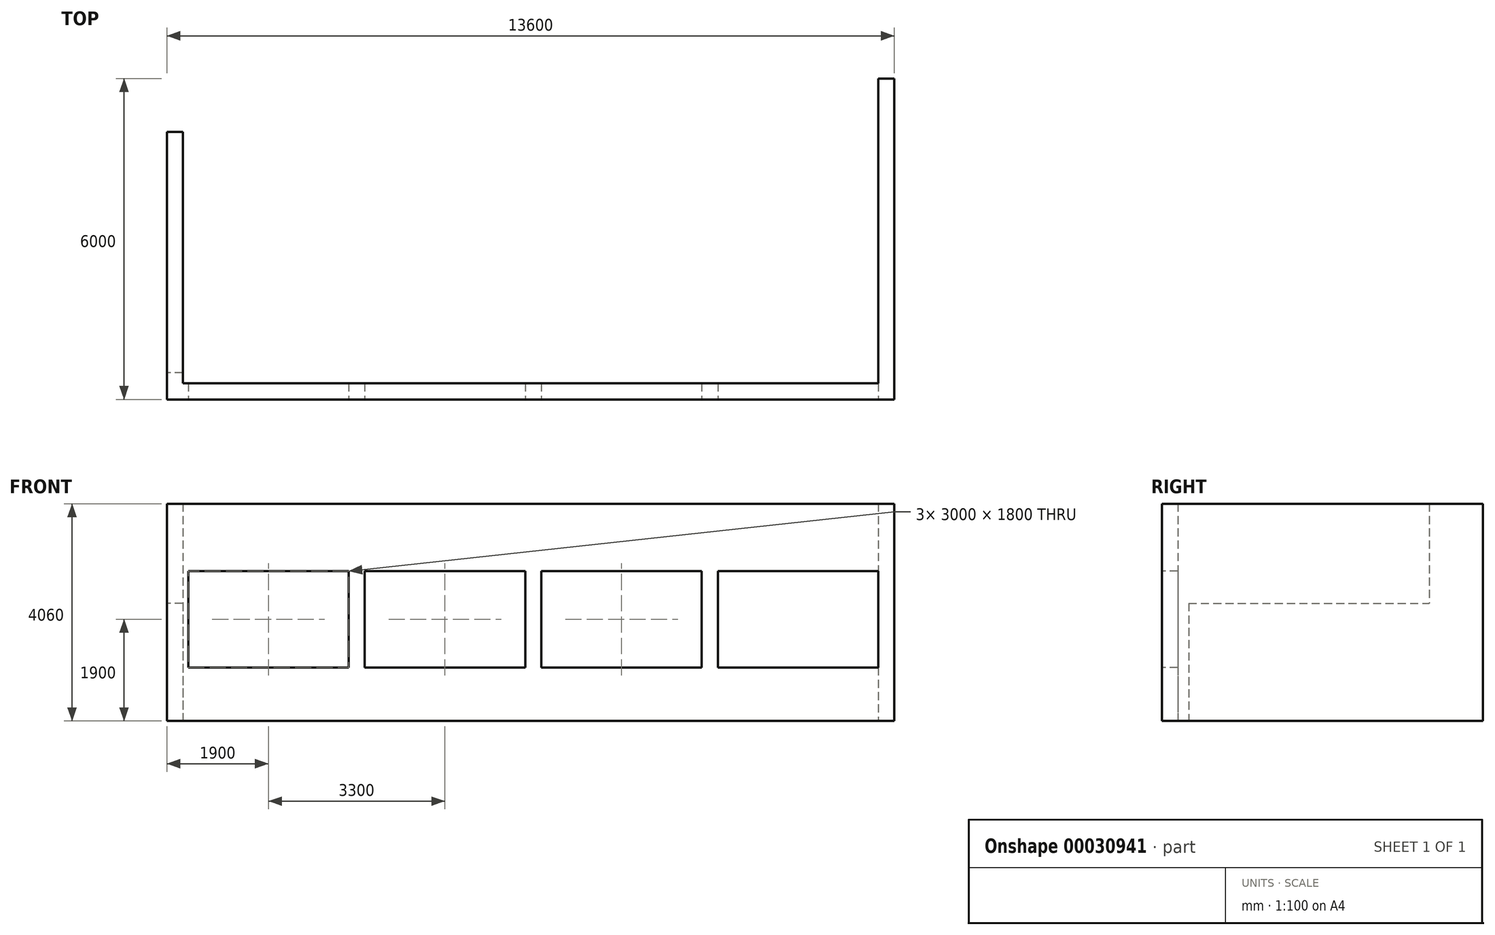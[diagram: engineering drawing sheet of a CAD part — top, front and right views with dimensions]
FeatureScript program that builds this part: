
annotation { "Feature Type Name" : "Feature", "Feature Type Description" : "" }
export const myFeature = defineFeature(function(context is Context, id is Id, definition is map)
    precondition{}
    {
        {
            var Q0;
            Q0=qCreatedBy(makeId("Top.planeOp"),FACE);
            var sketch = newSketch(context, id + "F0", { "sketchPlane" : qUnion([Q0])});
            skLineSegment(sketch, "E0", {"start": v(0, 0) * mm, "end": v(0, -5000) * mm});
            skLineSegment(sketch, "E1", {"start": v(0, -5000) * mm, "end": v(13600, -5000) * mm});
            skLineSegment(sketch, "E2", {"start": v(13600, -5000) * mm, "end": v(13600, 1000) * mm});
            skLineSegment(sketch, "E3.0", {"start": v(300, -4700) * mm, "end": v(13300, -4700) * mm});
            skLineSegment(sketch, "E3.1", {"start": v(300, 0) * mm, "end": v(300, -4700) * mm});
            skLineSegment(sketch, "E4.0", {"start": v(13300, -4700) * mm, "end": v(13300, 1000) * mm});
            skLineSegment(sketch, "E5", {"start": v(0, 0) * mm, "end": v(300, 0) * mm});
            skLineSegment(sketch, "E6", {"start": v(13300, 1000) * mm, "end": v(13600, 1000) * mm});
            skSolve(sketch);
        }
        {
            var Q0;
            Q0=makeQuery(id+"F0.imprint","IMPRINT",FACE,{"disambiguationData":[TD([[makeQuery(id+"F0.imprint","IMPRINT",EDGE,{"derivedFrom":sQuery(id+"F0.wireOp",EDGE,"E0")}),1.0]])]});
            extrude(context, id + "F1", {"entities" : qUnion([Q0]), "depth" : 4060 * mm});
        }
        {
            var Q0;
            Q0=makeQuery(id+"F1.opExtrude","SWEPT_FACE",FACE,{"disambiguationData":[OSD([sQuery(id+"F0.wireOp",EDGE,"E1")])]});
            var sketch = newSketch(context, id + "F2", { "sketchPlane" : qUnion([Q0])});
            skLineSegment(sketch, "E7.bottom", {"start": v(400, 2800) * mm, "end": v(3400, 2800) * mm});
            skLineSegment(sketch, "E7.top", {"start": v(400, 1000) * mm, "end": v(3400, 1000) * mm});
            skLineSegment(sketch, "E7.left", {"start": v(400, 2800) * mm, "end": v(400, 1000) * mm});
            skLineSegment(sketch, "E7.right", {"start": v(3400, 2800) * mm, "end": v(3400, 1000) * mm});
            skLineSegment(sketch, "E8.bottom", {"start": v(3700, 2800) * mm, "end": v(6700, 2800) * mm});
            skLineSegment(sketch, "E8.top", {"start": v(3700, 1000) * mm, "end": v(6700, 1000) * mm});
            skLineSegment(sketch, "E8.left", {"start": v(3700, 2800) * mm, "end": v(3700, 1000) * mm});
            skLineSegment(sketch, "E8.right", {"start": v(6700, 2800) * mm, "end": v(6700, 1000) * mm});
            skLineSegment(sketch, "E9.bottom", {"start": v(7000, 1000) * mm, "end": v(10000, 1000) * mm});
            skLineSegment(sketch, "E9.top", {"start": v(7000, 2800) * mm, "end": v(10000, 2800) * mm});
            skLineSegment(sketch, "E9.left", {"start": v(7000, 1000) * mm, "end": v(7000, 2800) * mm});
            skLineSegment(sketch, "E9.right", {"start": v(10000, 1000) * mm, "end": v(10000, 2800) * mm});
            skSolve(sketch);
        }
        {
            var Q0;
            Q0 = qSketchRegion(id + "F2", true);
            extrude(context, id + "F3", {"entities" : qUnion([Q0]), "operationType" : NewBodyOperationType.REMOVE, "endBound" : BoundingType.THROUGH_ALL, "oppositeDirection" : true, "depth" : 25 * mm});
        }
        {
            var Q0;
            Q0=makeQuery(id+"F1.opExtrude","SWEPT_FACE",FACE,{"disambiguationData":[OSD([sQuery(id+"F0.wireOp",EDGE,"E1")])]});
            var sketch = newSketch(context, id + "F4", { "sketchPlane" : qUnion([Q0])});
            skSolve(sketch);
        }
        {
            var Q0;
            Q0=makeQuery(id+"F1.opExtrude","SWEPT_FACE",FACE,{"disambiguationData":[OSD([sQuery(id+"F0.wireOp",EDGE,"E0")])]});
            var sketch = newSketch(context, id + "F5", { "sketchPlane" : qUnion([Q0])});
            skLineSegment(sketch, "E10.bottom", {"start": v(0, 0) * mm, "end": v(4500, 0) * mm});
            skLineSegment(sketch, "E10.top", {"start": v(0, 2200) * mm, "end": v(4500, 2200) * mm});
            skLineSegment(sketch, "E10.left", {"start": v(0, 0) * mm, "end": v(0, 2200) * mm});
            skLineSegment(sketch, "E10.right", {"start": v(4500, 0) * mm, "end": v(4500, 2200) * mm});
            skSolve(sketch);
        }
        {
            var Q0;
            Q0 = qSketchRegion(id + "F5", true);
            extrude(context, id + "F6", {"entities" : qUnion([Q0]), "operationType" : NewBodyOperationType.REMOVE, "oppositeDirection" : true, "depth" : 500 * mm});
        }
        {
            var Q0;
            {var subQ0=sQuery(id+"F0.wireOp",EDGE,"E1");Q0=makeQuery(id+"F4.imprint","IMPRINT",FACE,{"disambiguationData":[TD([[makeQuery(id+"F4.imprint","IMPRINT",EDGE,{"derivedFrom":makeQuery(id+"F1.opExtrude","CAP_EDGE",EDGE,{"disambiguationData":[OSD([subQ0])],"isStart":true})}),1.0]])]});}
            var sketch = newSketch(context, id + "F7", { "sketchPlane" : qUnion([Q0])});
            skLineSegment(sketch, "E11.bottom", {"start": v(10300, 2800) * mm, "end": v(13300, 2800) * mm});
            skLineSegment(sketch, "E11.top", {"start": v(10300, 1000) * mm, "end": v(13300, 1000) * mm});
            skLineSegment(sketch, "E11.left", {"start": v(10300, 2800) * mm, "end": v(10300, 1000) * mm});
            skLineSegment(sketch, "E11.right", {"start": v(13300, 2800) * mm, "end": v(13300, 1000) * mm});
            skSolve(sketch);
        }
        {
            var Q0;
            Q0 = qSketchRegion(id + "F7", true);
            extrude(context, id + "F8", {"entities" : qUnion([Q0]), "operationType" : NewBodyOperationType.REMOVE, "oppositeDirection" : true, "depth" : 500 * mm});
        }
    });
